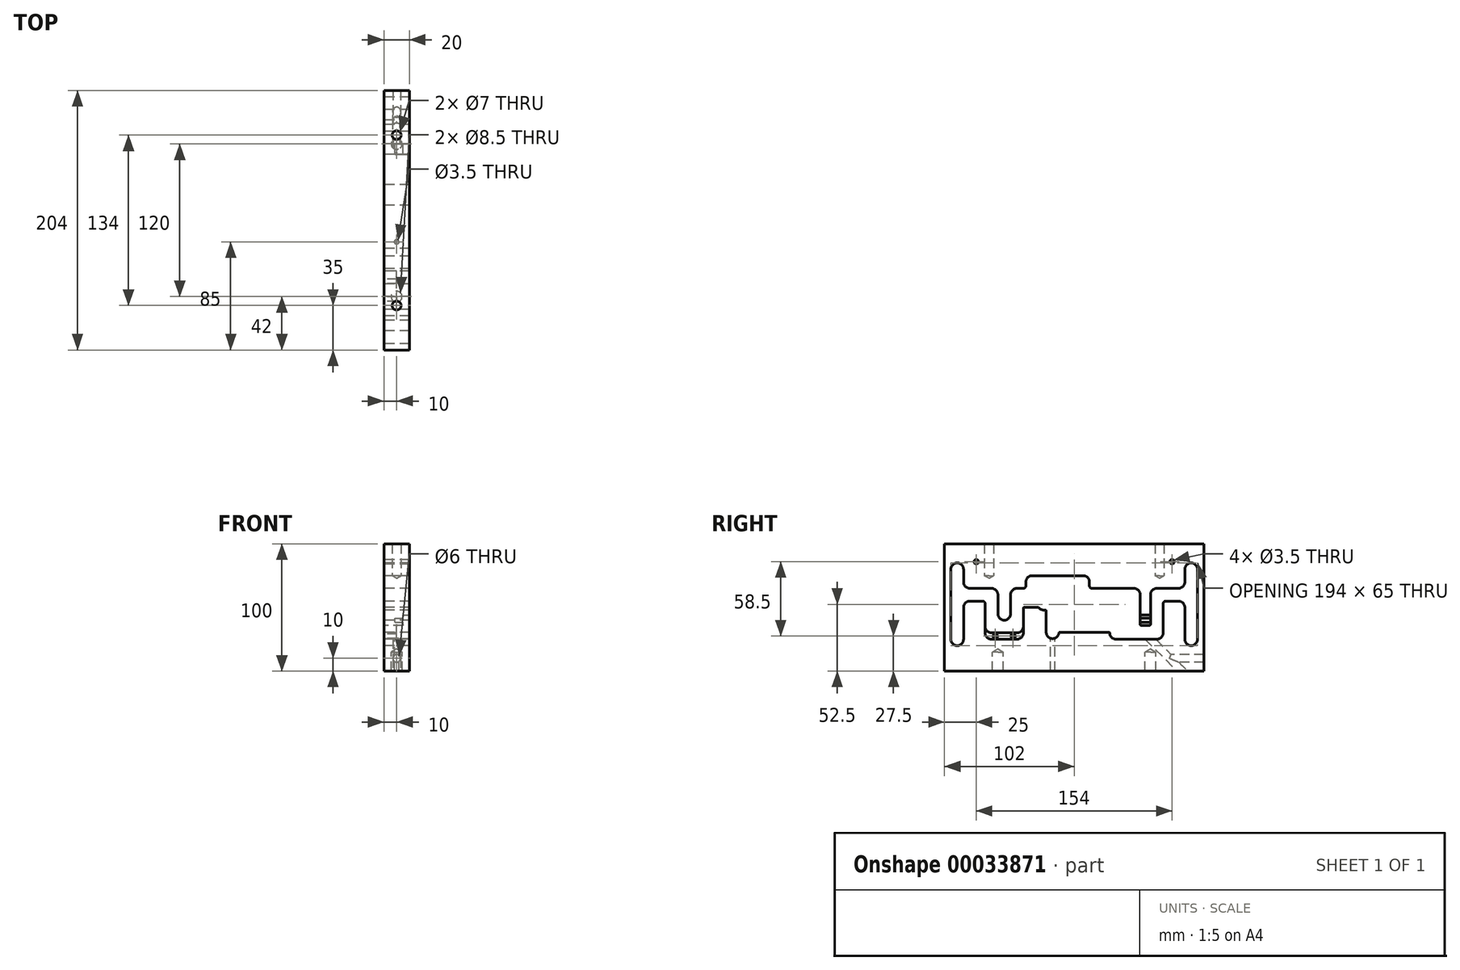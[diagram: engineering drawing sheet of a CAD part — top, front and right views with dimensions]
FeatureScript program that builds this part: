
annotation { "Feature Type Name" : "Feature", "Feature Type Description" : "" }
export const myFeature = defineFeature(function(context is Context, id is Id, definition is map)
    precondition{}
    {
        {
            var Q0;
            Q0=qCreatedBy(makeId("Right.planeOp"),FACE);
            var sketch = newSketch(context, id + "F0", { "sketchPlane" : qUnion([Q0])});
            skLineSegment(sketch, "E0.bottom", {"start": v(0, 0) * mm, "end": v(-204, 0) * mm});
            skLineSegment(sketch, "E0.top", {"start": v(0, 100) * mm, "end": v(-204, 100) * mm});
            skLineSegment(sketch, "E0.left", {"start": v(0, 0) * mm, "end": v(0, 100) * mm});
            skLineSegment(sketch, "E0.right", {"start": v(-204, 0) * mm, "end": v(-204, 100) * mm});
            skLineSegment(sketch, "E1", {"start": v(-167, 65) * mm, "end": v(-184, 65) * mm});
            skLineSegment(sketch, "E2", {"start": v(-189, 70) * mm, "end": v(-189, 80) * mm});
            skLineSegment(sketch, "E3", {"start": v(-199, 80) * mm, "end": v(-199, 25) * mm});
            skLineSegment(sketch, "E4", {"start": v(-189, 25) * mm, "end": v(-189, 50) * mm});
            skLineSegment(sketch, "E5", {"start": v(-184, 55) * mm, "end": v(-174, 55) * mm});
            skLineSegment(sketch, "E6", {"start": v(-172, 53) * mm, "end": v(-172, 30) * mm});
            skLineSegment(sketch, "E7", {"start": v(-167, 25) * mm, "end": v(-147, 25) * mm});
            skLineSegment(sketch, "E8", {"start": v(-142, 30) * mm, "end": v(-142, 49.5) * mm});
            skLineSegment(sketch, "E9", {"start": v(-114, 30.5) * mm, "end": v(-74, 30.5) * mm});
            skLineSegment(sketch, "E10", {"start": v(-69, 25) * mm, "end": v(-37, 25) * mm});
            skLineSegment(sketch, "E11", {"start": v(-32, 30) * mm, "end": v(-32, 53) * mm});
            skLineSegment(sketch, "E12", {"start": v(-30, 55) * mm, "end": v(-20, 55) * mm});
            skLineSegment(sketch, "E13", {"start": v(-15, 50) * mm, "end": v(-15, 25) * mm});
            skLineSegment(sketch, "E14", {"start": v(-5, 25) * mm, "end": v(-5, 80) * mm});
            skLineSegment(sketch, "E15", {"start": v(-15, 80) * mm, "end": v(-15, 70) * mm});
            skLineSegment(sketch, "E16", {"start": v(-20, 65) * mm, "end": v(-37, 65) * mm});
            skLineSegment(sketch, "E17", {"start": v(-42, 60) * mm, "end": v(-42, 36.5) * mm});
            skLineSegment(sketch, "E18", {"start": v(-42.5, 36) * mm, "end": v(-49.5, 36) * mm});
            skLineSegment(sketch, "E19", {"start": v(-50, 36.5) * mm, "end": v(-50, 60) * mm});
            skLineSegment(sketch, "E20", {"start": v(-152, 60) * mm, "end": v(-152, 45) * mm});
            skLineSegment(sketch, "E21", {"start": v(-162, 45) * mm, "end": v(-162, 60) * mm});
            skArc(sketch, "E22", {"start": v(-199, 25) * mm, "mid": v(-194, 20) * mm, "end": v(-189, 25) * mm});
            skArc(sketch, "E23", {"start": v(-189, 80) * mm, "mid": v(-194, 85) * mm, "end": v(-199, 80) * mm});
            skArc(sketch, "E24", {"start": v(-5, 80) * mm, "mid": v(-10, 85) * mm, "end": v(-15, 80) * mm});
            skArc(sketch, "E25", {"start": v(-15, 25) * mm, "mid": v(-10, 20) * mm, "end": v(-5, 25) * mm});
            skPoint(sketch, "E26.visualSharp", {"position": v(-189, 65) * mm});
            skArc(sketch, "E26.filletArc", {"start": v(-189, 70) * mm, "mid": v(-187.54, 66.46) * mm, "end": v(-184, 65) * mm});
            skPoint(sketch, "E27.visualSharp", {"position": v(-189, 55) * mm});
            skArc(sketch, "E27.filletArc", {"start": v(-184, 55) * mm, "mid": v(-187.54, 53.54) * mm, "end": v(-189, 50) * mm});
            skPoint(sketch, "E28.visualSharp", {"position": v(-15, 65) * mm});
            skArc(sketch, "E28.filletArc", {"start": v(-20, 65) * mm, "mid": v(-16.46, 66.46) * mm, "end": v(-15, 70) * mm});
            skPoint(sketch, "E29.visualSharp", {"position": v(-15, 55) * mm});
            skArc(sketch, "E29.filletArc", {"start": v(-15, 50) * mm, "mid": v(-16.46, 53.54) * mm, "end": v(-20, 55) * mm});
            skPoint(sketch, "E30.visualSharp", {"position": v(-162, 65) * mm});
            skArc(sketch, "E30.filletArc", {"start": v(-162, 60) * mm, "mid": v(-163.46, 63.54) * mm, "end": v(-167, 65) * mm});
            skPoint(sketch, "E31.visualSharp", {"position": v(-172, 25) * mm});
            skArc(sketch, "E31.filletArc", {"start": v(-172, 30) * mm, "mid": v(-170.54, 26.46) * mm, "end": v(-167, 25) * mm});
            skPoint(sketch, "E32.visualSharp", {"position": v(-142, 25) * mm});
            skArc(sketch, "E32.filletArc", {"start": v(-147, 25) * mm, "mid": v(-143.46, 26.46) * mm, "end": v(-142, 30) * mm});
            skArc(sketch, "E33", {"start": v(-162, 45) * mm, "mid": v(-157, 40) * mm, "end": v(-152, 45) * mm});
            skPoint(sketch, "E34.visualSharp", {"position": v(-42, 65) * mm});
            skArc(sketch, "E34.filletArc", {"start": v(-37, 65) * mm, "mid": v(-40.54, 63.54) * mm, "end": v(-42, 60) * mm});
            skLineSegment(sketch, "E35", {"start": v(-147, 65) * mm, "end": v(-142, 65) * mm});
            skLineSegment(sketch, "E36", {"start": v(-141.5, 50) * mm, "end": v(-130, 50) * mm});
            skPoint(sketch, "E37.visualSharp", {"position": v(-152, 65) * mm});
            skArc(sketch, "E37.filletArc", {"start": v(-147, 65) * mm, "mid": v(-150.54, 63.54) * mm, "end": v(-152, 60) * mm});
            skPoint(sketch, "E38.visualSharp", {"position": v(-172, 55) * mm});
            skArc(sketch, "E38.filletArc", {"start": v(-172, 53) * mm, "mid": v(-172.59, 54.41) * mm, "end": v(-174, 55) * mm});
            skPoint(sketch, "E39.visualSharp", {"position": v(-32, 55) * mm});
            skArc(sketch, "E39.filletArc", {"start": v(-30, 55) * mm, "mid": v(-31.41, 54.41) * mm, "end": v(-32, 53) * mm});
            skPoint(sketch, "E40.visualSharp", {"position": v(-32, 25) * mm});
            skArc(sketch, "E40.filletArc", {"start": v(-37, 25) * mm, "mid": v(-33.46, 26.46) * mm, "end": v(-32, 30) * mm});
            skLineSegment(sketch, "E41", {"start": v(-126, 48) * mm, "end": v(-124, 48) * mm});
            skLineSegment(sketch, "E42", {"start": v(-124, 48) * mm, "end": v(-124, 30.5) * mm});
            skArc(sketch, "E43", {"start": v(-124, 30.5) * mm, "mid": v(-119, 25.5) * mm, "end": v(-114, 30.5) * mm});
            skArc(sketch, "E44", {"start": v(-130, 50) * mm, "mid": v(-128.24, 48.53) * mm, "end": v(-126, 48) * mm});
            skLineSegment(sketch, "E45.bottom", {"start": v(-116.5, 49.5) * mm, "end": v(-63.5, 49.5) * mm, "construction": true});
            skLineSegment(sketch, "E45.top", {"start": v(-116.5, 30.5) * mm, "end": v(-63.5, 30.5) * mm, "construction": true});
            skLineSegment(sketch, "E45.left", {"start": v(-116.5, 49.5) * mm, "end": v(-116.5, 30.5) * mm, "construction": true});
            skLineSegment(sketch, "E45.right", {"start": v(-63.5, 49.5) * mm, "end": v(-63.5, 30.5) * mm, "construction": true});
            skLineSegment(sketch, "E46", {"start": v(-86.55, 40) * mm, "end": v(-38.27, 40) * mm, "construction": true});
            skPoint(sketch, "E46.startSnap0", {"position": v(-63.5, 40) * mm});
            skLineSegment(sketch, "E47", {"start": v(-74, 30.5) * mm, "end": v(-74, 30) * mm});
            skPoint(sketch, "E48.visualSharp", {"position": v(-74, 25) * mm});
            skArc(sketch, "E48.filletArc", {"start": v(-74, 30) * mm, "mid": v(-72.54, 26.46) * mm, "end": v(-69, 25) * mm});
            skPoint(sketch, "E49.visualSharp", {"position": v(-50, 65) * mm});
            skArc(sketch, "E49.filletArc", {"start": v(-50, 60) * mm, "mid": v(-51.46, 63.54) * mm, "end": v(-55, 65) * mm});
            skLineSegment(sketch, "E50", {"start": v(-135, 75) * mm, "end": v(-95, 75) * mm});
            skLineSegment(sketch, "E51", {"start": v(-90, 70) * mm, "end": v(-90, 67) * mm});
            skLineSegment(sketch, "E52", {"start": v(-140, 70) * mm, "end": v(-140, 67) * mm});
            skLineSegment(sketch, "E53.trimOffspring", {"start": v(-88, 65) * mm, "end": v(-55, 65) * mm});
            skPoint(sketch, "E54.visualSharp", {"position": v(-140, 75) * mm});
            skArc(sketch, "E54.filletArc", {"start": v(-135, 75) * mm, "mid": v(-138.54, 73.54) * mm, "end": v(-140, 70) * mm});
            skPoint(sketch, "E55.visualSharp", {"position": v(-90, 75) * mm});
            skArc(sketch, "E55.filletArc", {"start": v(-90, 70) * mm, "mid": v(-91.46, 73.54) * mm, "end": v(-95, 75) * mm});
            skPoint(sketch, "E56.visualSharp", {"position": v(-140, 65) * mm});
            skArc(sketch, "E56.filletArc", {"start": v(-142, 65) * mm, "mid": v(-140.59, 65.59) * mm, "end": v(-140, 67) * mm});
            skPoint(sketch, "E57.visualSharp", {"position": v(-90, 65) * mm});
            skArc(sketch, "E57.filletArc", {"start": v(-90, 67) * mm, "mid": v(-89.41, 65.59) * mm, "end": v(-88, 65) * mm});
            skLineSegment(sketch, "E58", {"start": v(-179, 86) * mm, "end": v(-25, 86) * mm, "construction": true});
            skCircle(sketch, "E59", {"center": v(-179, 86) * mm, "radius": 1.75 * mm});
            skCircle(sketch, "E60", {"center": v(-25, 86) * mm, "radius": 1.75 * mm});
            skLineSegment(sketch, "E61", {"start": v(-147, 30) * mm, "end": v(-167, 30) * mm});
            skPoint(sketch, "E62.visualSharp", {"position": v(-172, 30) * mm});
            skArc(sketch, "E62.filletArc", {"start": v(-172, 35) * mm, "mid": v(-170.54, 31.46) * mm, "end": v(-167, 30) * mm});
            skPoint(sketch, "E63.visualSharp", {"position": v(-142, 30) * mm});
            skArc(sketch, "E63.filletArc", {"start": v(-147, 30) * mm, "mid": v(-143.46, 31.46) * mm, "end": v(-142, 35) * mm});
            skCircle(sketch, "E64", {"center": v(-150, 27.5) * mm, "radius": 1.75 * mm});
            skCircle(sketch, "E65", {"center": v(-164, 27.5) * mm, "radius": 1.75 * mm});
            skLineSegment(sketch, "E66", {"start": v(-157, 28.47) * mm, "end": v(-157, 26.58) * mm, "construction": true});
            skPoint(sketch, "E66.startSnap0", {"position": v(-157, 30) * mm});
            skPoint(sketch, "E67.visualSharp", {"position": v(-142, 50) * mm});
            skArc(sketch, "E67.filletArc", {"start": v(-141.5, 50) * mm, "mid": v(-141.85, 49.85) * mm, "end": v(-142, 49.5) * mm});
            skPoint(sketch, "E68.visualSharp", {"position": v(-42, 36) * mm});
            skArc(sketch, "E68.filletArc", {"start": v(-42.5, 36) * mm, "mid": v(-42.15, 36.15) * mm, "end": v(-42, 36.5) * mm});
            skPoint(sketch, "E69.visualSharp", {"position": v(-50, 36) * mm});
            skArc(sketch, "E69.filletArc", {"start": v(-50, 36.5) * mm, "mid": v(-49.85, 36.15) * mm, "end": v(-49.5, 36) * mm});
            skSolve(sketch);
        }
        {
            var Q0;
            Q0 = qSketchRegion(id + "F0", true);
            extrude(context, id + "F1", {"entities" : qUnion([Q0]), "depth" : 20 * mm});
        }
        {
            var Q0;
            Q0=makeQuery(id+"F1.opExtrude","SWEPT_FACE",FACE,{"disambiguationData":[OSD([sQuery(id+"F0.wireOp",EDGE,"E0.bottom")])]});
            var sketch = newSketch(context, id + "F2", { "sketchPlane" : qUnion([Q0])});
            skPoint(sketch, "E70", {"position": v(10, 119) * mm});
            skPoint(sketch, "E70.positionSnap0", {"position": v(10, 204) * mm});
            skSolve(sketch);
        }
        {
            var Q0;
            Q0=sQuery(id+"F2.wireOp",VERTEX,"E70");
            var Q1;
            Q1=makeQuery(id+"F1.opExtrude","SWEPT_BODY",BODY,{"disambiguationData":[OSD([sQuery(id+"F0.wireOp",EDGE,"E0.bottom"),sQuery(id+"F0.wireOp",EDGE,"E0.top"),sQuery(id+"F0.wireOp",EDGE,"E0.left"),sQuery(id+"F0.wireOp",EDGE,"E0.right"),sQuery(id+"F0.wireOp",EDGE,"E1"),sQuery(id+"F0.wireOp",EDGE,"E2"),sQuery(id+"F0.wireOp",EDGE,"E3"),sQuery(id+"F0.wireOp",EDGE,"E4"),sQuery(id+"F0.wireOp",EDGE,"E5"),sQuery(id+"F0.wireOp",EDGE,"E6"),sQuery(id+"F0.wireOp",EDGE,"E7"),sQuery(id+"F0.wireOp",EDGE,"E8"),sQuery(id+"F0.wireOp",EDGE,"E9"),sQuery(id+"F0.wireOp",EDGE,"E10"),sQuery(id+"F0.wireOp",EDGE,"E11"),sQuery(id+"F0.wireOp",EDGE,"E12"),sQuery(id+"F0.wireOp",EDGE,"E13"),sQuery(id+"F0.wireOp",EDGE,"E14"),sQuery(id+"F0.wireOp",EDGE,"E15"),sQuery(id+"F0.wireOp",EDGE,"E16"),sQuery(id+"F0.wireOp",EDGE,"E17"),sQuery(id+"F0.wireOp",EDGE,"E18"),sQuery(id+"F0.wireOp",EDGE,"E19"),sQuery(id+"F0.wireOp",EDGE,"E20"),sQuery(id+"F0.wireOp",EDGE,"E21"),sQuery(id+"F0.wireOp",EDGE,"E22"),sQuery(id+"F0.wireOp",EDGE,"E23"),sQuery(id+"F0.wireOp",EDGE,"E24"),sQuery(id+"F0.wireOp",EDGE,"E25"),sQuery(id+"F0.wireOp",EDGE,"E26.filletArc"),sQuery(id+"F0.wireOp",EDGE,"E27.filletArc"),sQuery(id+"F0.wireOp",EDGE,"E28.filletArc"),sQuery(id+"F0.wireOp",EDGE,"E29.filletArc"),sQuery(id+"F0.wireOp",EDGE,"E30.filletArc"),sQuery(id+"F0.wireOp",EDGE,"E31.filletArc"),sQuery(id+"F0.wireOp",EDGE,"E32.filletArc"),sQuery(id+"F0.wireOp",EDGE,"E33"),sQuery(id+"F0.wireOp",EDGE,"E34.filletArc"),sQuery(id+"F0.wireOp",EDGE,"E35"),sQuery(id+"F0.wireOp",EDGE,"E36"),sQuery(id+"F0.wireOp",EDGE,"E37.filletArc"),sQuery(id+"F0.wireOp",EDGE,"E38.filletArc"),sQuery(id+"F0.wireOp",EDGE,"E39.filletArc"),sQuery(id+"F0.wireOp",EDGE,"E40.filletArc"),sQuery(id+"F0.wireOp",EDGE,"E41"),sQuery(id+"F0.wireOp",EDGE,"E42"),sQuery(id+"F0.wireOp",EDGE,"E43"),sQuery(id+"F0.wireOp",EDGE,"E44"),sQuery(id+"F0.wireOp",EDGE,"E47"),sQuery(id+"F0.wireOp",EDGE,"E48.filletArc"),sQuery(id+"F0.wireOp",EDGE,"E49.filletArc"),sQuery(id+"F0.wireOp",EDGE,"E50"),sQuery(id+"F0.wireOp",EDGE,"E51"),sQuery(id+"F0.wireOp",EDGE,"E52"),sQuery(id+"F0.wireOp",EDGE,"E53.trimOffspring"),sQuery(id+"F0.wireOp",EDGE,"E54.filletArc"),sQuery(id+"F0.wireOp",EDGE,"E55.filletArc"),sQuery(id+"F0.wireOp",EDGE,"E56.filletArc"),sQuery(id+"F0.wireOp",EDGE,"E57.filletArc")])]});
            hole(context, id + "F3", {"style" : HoleStyle.SIMPLE, "holeDiameter" : 3.5 * mm, "endStyle" : HoleEndStyle.BLIND, "holeDepth" : 30 * mm, "locations" : qUnion([Q0]), "scope" : qUnion([Q1])});
        }
        {
            var Q0;
            Q0=makeQuery(id+"F1.opExtrude","SWEPT_FACE",FACE,{"disambiguationData":[OSD([sQuery(id+"F0.wireOp",EDGE,"E0.top")])]});
            var sketch = newSketch(context, id + "F4", { "sketchPlane" : qUnion([Q0])});
            skPoint(sketch, "E71", {"position": v(10, -169) * mm});
            skPoint(sketch, "E71.positionSnap0", {"position": v(10, -204) * mm});
            skPoint(sketch, "E72", {"position": v(10, -35) * mm});
            skPoint(sketch, "E72.positionSnap0", {"position": v(10, 0) * mm});
            skSolve(sketch);
        }
        {
            var Q0;
            Q0=sQuery(id+"F4.wireOp",VERTEX,"E71");
            var Q1;
            Q1=sQuery(id+"F4.wireOp",VERTEX,"E72");
            var Q2;
            Q2=makeQuery(id+"F1.opExtrude","SWEPT_BODY",BODY,{"disambiguationData":[OSD([sQuery(id+"F0.wireOp",EDGE,"E0.bottom"),sQuery(id+"F0.wireOp",EDGE,"E0.top"),sQuery(id+"F0.wireOp",EDGE,"E0.left"),sQuery(id+"F0.wireOp",EDGE,"E0.right"),sQuery(id+"F0.wireOp",EDGE,"E1"),sQuery(id+"F0.wireOp",EDGE,"E2"),sQuery(id+"F0.wireOp",EDGE,"E3"),sQuery(id+"F0.wireOp",EDGE,"E4"),sQuery(id+"F0.wireOp",EDGE,"E5"),sQuery(id+"F0.wireOp",EDGE,"E6"),sQuery(id+"F0.wireOp",EDGE,"E7"),sQuery(id+"F0.wireOp",EDGE,"E8"),sQuery(id+"F0.wireOp",EDGE,"E9"),sQuery(id+"F0.wireOp",EDGE,"E10"),sQuery(id+"F0.wireOp",EDGE,"E11"),sQuery(id+"F0.wireOp",EDGE,"E12"),sQuery(id+"F0.wireOp",EDGE,"E13"),sQuery(id+"F0.wireOp",EDGE,"E14"),sQuery(id+"F0.wireOp",EDGE,"E15"),sQuery(id+"F0.wireOp",EDGE,"E16"),sQuery(id+"F0.wireOp",EDGE,"E17"),sQuery(id+"F0.wireOp",EDGE,"E18"),sQuery(id+"F0.wireOp",EDGE,"E19"),sQuery(id+"F0.wireOp",EDGE,"E20"),sQuery(id+"F0.wireOp",EDGE,"E21"),sQuery(id+"F0.wireOp",EDGE,"E22"),sQuery(id+"F0.wireOp",EDGE,"E23"),sQuery(id+"F0.wireOp",EDGE,"E24"),sQuery(id+"F0.wireOp",EDGE,"E25"),sQuery(id+"F0.wireOp",EDGE,"E26.filletArc"),sQuery(id+"F0.wireOp",EDGE,"E27.filletArc"),sQuery(id+"F0.wireOp",EDGE,"E28.filletArc"),sQuery(id+"F0.wireOp",EDGE,"E29.filletArc"),sQuery(id+"F0.wireOp",EDGE,"E30.filletArc"),sQuery(id+"F0.wireOp",EDGE,"E31.filletArc"),sQuery(id+"F0.wireOp",EDGE,"E32.filletArc"),sQuery(id+"F0.wireOp",EDGE,"E33"),sQuery(id+"F0.wireOp",EDGE,"E34.filletArc"),sQuery(id+"F0.wireOp",EDGE,"E35"),sQuery(id+"F0.wireOp",EDGE,"E36"),sQuery(id+"F0.wireOp",EDGE,"E37.filletArc"),sQuery(id+"F0.wireOp",EDGE,"E38.filletArc"),sQuery(id+"F0.wireOp",EDGE,"E39.filletArc"),sQuery(id+"F0.wireOp",EDGE,"E40.filletArc"),sQuery(id+"F0.wireOp",EDGE,"E41"),sQuery(id+"F0.wireOp",EDGE,"E42"),sQuery(id+"F0.wireOp",EDGE,"E43"),sQuery(id+"F0.wireOp",EDGE,"E44"),sQuery(id+"F0.wireOp",EDGE,"E47"),sQuery(id+"F0.wireOp",EDGE,"E48.filletArc"),sQuery(id+"F0.wireOp",EDGE,"E49.filletArc"),sQuery(id+"F0.wireOp",EDGE,"E50"),sQuery(id+"F0.wireOp",EDGE,"E51"),sQuery(id+"F0.wireOp",EDGE,"E52"),sQuery(id+"F0.wireOp",EDGE,"E53.trimOffspring"),sQuery(id+"F0.wireOp",EDGE,"E54.filletArc"),sQuery(id+"F0.wireOp",EDGE,"E55.filletArc"),sQuery(id+"F0.wireOp",EDGE,"E56.filletArc"),sQuery(id+"F0.wireOp",EDGE,"E57.filletArc")])]});
            hole(context, id + "F5", {"style" : HoleStyle.SIMPLE, "holeDiameter" : 7 * mm, "endStyle" : HoleEndStyle.BLIND, "holeDepth" : 25 * mm, "locations" : qUnion([Q0, Q1]), "scope" : qUnion([Q2])});
        }
        {
            var Q0;
            Q0=makeQuery(id+"F1.opExtrude","SWEPT_FACE",FACE,{"disambiguationData":[OSD([sQuery(id+"F0.wireOp",EDGE,"E0.left")])]});
            var sketch = newSketch(context, id + "F6", { "sketchPlane" : qUnion([Q0])});
            skPoint(sketch, "E73", {"position": v(-10, 10) * mm});
            skPoint(sketch, "E73.positionSnap0", {"position": v(-10, 0) * mm});
            skSolve(sketch);
        }
        {
            var Q0;
            Q0=sQuery(id+"F6.wireOp",VERTEX,"E73");
            var Q1;
            Q1=makeQuery(id+"F1.opExtrude","SWEPT_BODY",BODY,{"disambiguationData":[OSD([sQuery(id+"F0.wireOp",EDGE,"E0.bottom"),sQuery(id+"F0.wireOp",EDGE,"E0.top"),sQuery(id+"F0.wireOp",EDGE,"E0.left"),sQuery(id+"F0.wireOp",EDGE,"E0.right"),sQuery(id+"F0.wireOp",EDGE,"E1"),sQuery(id+"F0.wireOp",EDGE,"E2"),sQuery(id+"F0.wireOp",EDGE,"E3"),sQuery(id+"F0.wireOp",EDGE,"E4"),sQuery(id+"F0.wireOp",EDGE,"E5"),sQuery(id+"F0.wireOp",EDGE,"E6"),sQuery(id+"F0.wireOp",EDGE,"E7"),sQuery(id+"F0.wireOp",EDGE,"E8"),sQuery(id+"F0.wireOp",EDGE,"E9"),sQuery(id+"F0.wireOp",EDGE,"E10"),sQuery(id+"F0.wireOp",EDGE,"E11"),sQuery(id+"F0.wireOp",EDGE,"E12"),sQuery(id+"F0.wireOp",EDGE,"E13"),sQuery(id+"F0.wireOp",EDGE,"E14"),sQuery(id+"F0.wireOp",EDGE,"E15"),sQuery(id+"F0.wireOp",EDGE,"E16"),sQuery(id+"F0.wireOp",EDGE,"E17"),sQuery(id+"F0.wireOp",EDGE,"E18"),sQuery(id+"F0.wireOp",EDGE,"E19"),sQuery(id+"F0.wireOp",EDGE,"E20"),sQuery(id+"F0.wireOp",EDGE,"E21"),sQuery(id+"F0.wireOp",EDGE,"E22"),sQuery(id+"F0.wireOp",EDGE,"E23"),sQuery(id+"F0.wireOp",EDGE,"E24"),sQuery(id+"F0.wireOp",EDGE,"E25"),sQuery(id+"F0.wireOp",EDGE,"E26.filletArc"),sQuery(id+"F0.wireOp",EDGE,"E27.filletArc"),sQuery(id+"F0.wireOp",EDGE,"E28.filletArc"),sQuery(id+"F0.wireOp",EDGE,"E29.filletArc"),sQuery(id+"F0.wireOp",EDGE,"E30.filletArc"),sQuery(id+"F0.wireOp",EDGE,"E31.filletArc"),sQuery(id+"F0.wireOp",EDGE,"E32.filletArc"),sQuery(id+"F0.wireOp",EDGE,"E33"),sQuery(id+"F0.wireOp",EDGE,"E34.filletArc"),sQuery(id+"F0.wireOp",EDGE,"E35"),sQuery(id+"F0.wireOp",EDGE,"E36"),sQuery(id+"F0.wireOp",EDGE,"E37.filletArc"),sQuery(id+"F0.wireOp",EDGE,"E38.filletArc"),sQuery(id+"F0.wireOp",EDGE,"E39.filletArc"),sQuery(id+"F0.wireOp",EDGE,"E40.filletArc"),sQuery(id+"F0.wireOp",EDGE,"E41"),sQuery(id+"F0.wireOp",EDGE,"E42"),sQuery(id+"F0.wireOp",EDGE,"E43"),sQuery(id+"F0.wireOp",EDGE,"E44"),sQuery(id+"F0.wireOp",EDGE,"E47"),sQuery(id+"F0.wireOp",EDGE,"E48.filletArc"),sQuery(id+"F0.wireOp",EDGE,"E49.filletArc"),sQuery(id+"F0.wireOp",EDGE,"E50"),sQuery(id+"F0.wireOp",EDGE,"E51"),sQuery(id+"F0.wireOp",EDGE,"E52"),sQuery(id+"F0.wireOp",EDGE,"E53.trimOffspring"),sQuery(id+"F0.wireOp",EDGE,"E54.filletArc"),sQuery(id+"F0.wireOp",EDGE,"E55.filletArc"),sQuery(id+"F0.wireOp",EDGE,"E56.filletArc"),sQuery(id+"F0.wireOp",EDGE,"E57.filletArc")])]});
            hole(context, id + "F7", {"style" : HoleStyle.SIMPLE, "holeDiameter" : 6 * mm, "endStyle" : HoleEndStyle.BLIND, "holeDepth" : 27 * mm, "locations" : qUnion([Q0]), "scope" : qUnion([Q1])});
        }
        {
            var Q0;
            Q0=makeQuery(id+"F1.opExtrude","SWEPT_EDGE",EDGE,{"disambiguationData":[OSD([sQuery(id+"F0.wireOp",EDGE,"E0.bottom"),sQuery(id+"F0.wireOp",EDGE,"E0.left")])]});
            cPlane(context, id + "F8", {"entities" : qUnion([Q0]), "cplaneType" : CPlaneType.LINE_ANGLE, "offset" : 150 * mm, "angle" : 45 * degree, "width" : 150 * mm, "height" : 150 * mm});
        }
        {
            var Q0;
            Q0=qCreatedBy(id+"F8.planeOp",FACE);
            var sketch = newSketch(context, id + "F9", { "sketchPlane" : qUnion([Q0])});
            skCircle(sketch, "E74", {"center": v(10, -12) * mm, "radius": 3 * mm});
            skSolve(sketch);
        }
        {
            var Q0;
            Q0=makeQuery(id+"F9.imprint","IMPRINT",FACE,{"disambiguationData":[TD([[makeQuery(id+"F9.imprint","IMPRINT",EDGE,{"derivedFrom":sQuery(id+"F9.wireOp",EDGE,"E74")}),1.0]])]});
            extrude(context, id + "F10", {"entities" : qUnion([Q0]), "operationType" : NewBodyOperationType.REMOVE, "depth" : 60 * mm});
        }
        {
            var Q0;
            Q0=makeQuery(id+"F1.opExtrude","SWEPT_FACE",FACE,{"disambiguationData":[OSD([sQuery(id+"F0.wireOp",EDGE,"E0.bottom")])]});
            var sketch = newSketch(context, id + "F11", { "sketchPlane" : qUnion([Q0])});
            skPoint(sketch, "E75", {"position": v(10, 42) * mm});
            skPoint(sketch, "E75.positionSnap0", {"position": v(10, 12.73) * mm});
            skPoint(sketch, "E76", {"position": v(10, 162) * mm});
            skPoint(sketch, "E76.positionSnap0", {"position": v(10, 204) * mm});
            skSolve(sketch);
        }
        {
            var Q0;
            Q0=sQuery(id+"F11.wireOp",VERTEX,"E76");
            var Q1;
            Q1=sQuery(id+"F11.wireOp",VERTEX,"E75");
            var Q2;
            Q2=makeQuery(id+"F1.opExtrude","SWEPT_BODY",BODY,{"disambiguationData":[OSD([sQuery(id+"F0.wireOp",EDGE,"E0.bottom"),sQuery(id+"F0.wireOp",EDGE,"E0.top"),sQuery(id+"F0.wireOp",EDGE,"E0.left"),sQuery(id+"F0.wireOp",EDGE,"E0.right"),sQuery(id+"F0.wireOp",EDGE,"E1"),sQuery(id+"F0.wireOp",EDGE,"E2"),sQuery(id+"F0.wireOp",EDGE,"E3"),sQuery(id+"F0.wireOp",EDGE,"E4"),sQuery(id+"F0.wireOp",EDGE,"E5"),sQuery(id+"F0.wireOp",EDGE,"E6"),sQuery(id+"F0.wireOp",EDGE,"E7"),sQuery(id+"F0.wireOp",EDGE,"E8"),sQuery(id+"F0.wireOp",EDGE,"E9"),sQuery(id+"F0.wireOp",EDGE,"E10"),sQuery(id+"F0.wireOp",EDGE,"E11"),sQuery(id+"F0.wireOp",EDGE,"E12"),sQuery(id+"F0.wireOp",EDGE,"E13"),sQuery(id+"F0.wireOp",EDGE,"E14"),sQuery(id+"F0.wireOp",EDGE,"E15"),sQuery(id+"F0.wireOp",EDGE,"E16"),sQuery(id+"F0.wireOp",EDGE,"E17"),sQuery(id+"F0.wireOp",EDGE,"E18"),sQuery(id+"F0.wireOp",EDGE,"E19"),sQuery(id+"F0.wireOp",EDGE,"E20"),sQuery(id+"F0.wireOp",EDGE,"E21"),sQuery(id+"F0.wireOp",EDGE,"E22"),sQuery(id+"F0.wireOp",EDGE,"E23"),sQuery(id+"F0.wireOp",EDGE,"E24"),sQuery(id+"F0.wireOp",EDGE,"E25"),sQuery(id+"F0.wireOp",EDGE,"E26.filletArc"),sQuery(id+"F0.wireOp",EDGE,"E27.filletArc"),sQuery(id+"F0.wireOp",EDGE,"E28.filletArc"),sQuery(id+"F0.wireOp",EDGE,"E29.filletArc"),sQuery(id+"F0.wireOp",EDGE,"E30.filletArc"),sQuery(id+"F0.wireOp",EDGE,"E31.filletArc"),sQuery(id+"F0.wireOp",EDGE,"E32.filletArc"),sQuery(id+"F0.wireOp",EDGE,"E33"),sQuery(id+"F0.wireOp",EDGE,"E34.filletArc"),sQuery(id+"F0.wireOp",EDGE,"E35"),sQuery(id+"F0.wireOp",EDGE,"E36"),sQuery(id+"F0.wireOp",EDGE,"E37.filletArc"),sQuery(id+"F0.wireOp",EDGE,"E38.filletArc"),sQuery(id+"F0.wireOp",EDGE,"E39.filletArc"),sQuery(id+"F0.wireOp",EDGE,"E40.filletArc"),sQuery(id+"F0.wireOp",EDGE,"E41"),sQuery(id+"F0.wireOp",EDGE,"E42"),sQuery(id+"F0.wireOp",EDGE,"E43"),sQuery(id+"F0.wireOp",EDGE,"E44"),sQuery(id+"F0.wireOp",EDGE,"E47"),sQuery(id+"F0.wireOp",EDGE,"E48.filletArc"),sQuery(id+"F0.wireOp",EDGE,"E49.filletArc"),sQuery(id+"F0.wireOp",EDGE,"E50"),sQuery(id+"F0.wireOp",EDGE,"E51"),sQuery(id+"F0.wireOp",EDGE,"E52"),sQuery(id+"F0.wireOp",EDGE,"E53.trimOffspring"),sQuery(id+"F0.wireOp",EDGE,"E54.filletArc"),sQuery(id+"F0.wireOp",EDGE,"E55.filletArc"),sQuery(id+"F0.wireOp",EDGE,"E56.filletArc"),sQuery(id+"F0.wireOp",EDGE,"E57.filletArc")])]});
            hole(context, id + "F12", {"style" : HoleStyle.SIMPLE, "holeDiameter" : 8.5 * mm, "endStyle" : HoleEndStyle.BLIND, "holeDepth" : 15 * mm, "locations" : qUnion([Q0, Q1]), "scope" : qUnion([Q2])});
        }
        {
            var Q0;
            Q0=makeQuery(id+"F0.imprint","IMPRINT",FACE,{"disambiguationData":[TD([[makeQuery(id+"F0.imprint","IMPRINT",EDGE,{"derivedFrom":sQuery(id+"F0.wireOp",EDGE,"E7")}),1.0]])]});
            extrude(context, id + "F13", {"entities" : qUnion([Q0]), "operationType" : NewBodyOperationType.ADD, "depth" : 10 * mm});
        }
        {
            var Q0;
            Q0=makeQuery(id+"F1.opExtrude","CAP_FACE",FACE,{"disambiguationData":[OSD([sQuery(id+"F0.wireOp",EDGE,"E0.bottom"),sQuery(id+"F0.wireOp",EDGE,"E0.top"),sQuery(id+"F0.wireOp",EDGE,"E0.left"),sQuery(id+"F0.wireOp",EDGE,"E0.right"),sQuery(id+"F0.wireOp",EDGE,"E1"),sQuery(id+"F0.wireOp",EDGE,"E2"),sQuery(id+"F0.wireOp",EDGE,"E3"),sQuery(id+"F0.wireOp",EDGE,"E4"),sQuery(id+"F0.wireOp",EDGE,"E5"),sQuery(id+"F0.wireOp",EDGE,"E6"),sQuery(id+"F0.wireOp",EDGE,"E7"),sQuery(id+"F0.wireOp",EDGE,"E8"),sQuery(id+"F0.wireOp",EDGE,"E9"),sQuery(id+"F0.wireOp",EDGE,"E10"),sQuery(id+"F0.wireOp",EDGE,"E11"),sQuery(id+"F0.wireOp",EDGE,"E12"),sQuery(id+"F0.wireOp",EDGE,"E13"),sQuery(id+"F0.wireOp",EDGE,"E14"),sQuery(id+"F0.wireOp",EDGE,"E15"),sQuery(id+"F0.wireOp",EDGE,"E16"),sQuery(id+"F0.wireOp",EDGE,"E17"),sQuery(id+"F0.wireOp",EDGE,"E18"),sQuery(id+"F0.wireOp",EDGE,"E19"),sQuery(id+"F0.wireOp",EDGE,"E20"),sQuery(id+"F0.wireOp",EDGE,"E21"),sQuery(id+"F0.wireOp",EDGE,"E22"),sQuery(id+"F0.wireOp",EDGE,"E23"),sQuery(id+"F0.wireOp",EDGE,"E24"),sQuery(id+"F0.wireOp",EDGE,"E25"),sQuery(id+"F0.wireOp",EDGE,"E26.filletArc"),sQuery(id+"F0.wireOp",EDGE,"E27.filletArc"),sQuery(id+"F0.wireOp",EDGE,"E28.filletArc"),sQuery(id+"F0.wireOp",EDGE,"E29.filletArc"),sQuery(id+"F0.wireOp",EDGE,"E30.filletArc"),sQuery(id+"F0.wireOp",EDGE,"E31.filletArc"),sQuery(id+"F0.wireOp",EDGE,"E32.filletArc"),sQuery(id+"F0.wireOp",EDGE,"E33"),sQuery(id+"F0.wireOp",EDGE,"E34.filletArc"),sQuery(id+"F0.wireOp",EDGE,"E35"),sQuery(id+"F0.wireOp",EDGE,"E36"),sQuery(id+"F0.wireOp",EDGE,"E37.filletArc"),sQuery(id+"F0.wireOp",EDGE,"E38.filletArc"),sQuery(id+"F0.wireOp",EDGE,"E39.filletArc"),sQuery(id+"F0.wireOp",EDGE,"E40.filletArc"),sQuery(id+"F0.wireOp",EDGE,"E41"),sQuery(id+"F0.wireOp",EDGE,"E42"),sQuery(id+"F0.wireOp",EDGE,"E43"),sQuery(id+"F0.wireOp",EDGE,"E44"),sQuery(id+"F0.wireOp",EDGE,"E47"),sQuery(id+"F0.wireOp",EDGE,"E48.filletArc"),sQuery(id+"F0.wireOp",EDGE,"E49.filletArc"),sQuery(id+"F0.wireOp",EDGE,"E50"),sQuery(id+"F0.wireOp",EDGE,"E51"),sQuery(id+"F0.wireOp",EDGE,"E52"),sQuery(id+"F0.wireOp",EDGE,"E53.trimOffspring"),sQuery(id+"F0.wireOp",EDGE,"E54.filletArc"),sQuery(id+"F0.wireOp",EDGE,"E55.filletArc"),sQuery(id+"F0.wireOp",EDGE,"E56.filletArc"),sQuery(id+"F0.wireOp",EDGE,"E57.filletArc"),sQuery(id+"F0.wireOp",EDGE,"E59"),sQuery(id+"F0.wireOp",EDGE,"E60")])],"isStart":false});
            var sketch = newSketch(context, id + "F14", { "sketchPlane" : qUnion([Q0])});
            skLineSegment(sketch, "E77.bottom", {"start": v(-50, 36) * mm, "end": v(-42, 36) * mm});
            skLineSegment(sketch, "E77.top", {"start": v(-50, 44) * mm, "end": v(-42, 44) * mm});
            skLineSegment(sketch, "E77.left", {"start": v(-50, 36) * mm, "end": v(-50, 44) * mm});
            skLineSegment(sketch, "E77.right", {"start": v(-42, 36) * mm, "end": v(-42, 44) * mm});
            skLineSegment(sketch, "E78.bottom", {"start": v(-50, 41.5) * mm, "end": v(-42, 41.5) * mm});
            skLineSegment(sketch, "E78.top", {"start": v(-50, 38.5) * mm, "end": v(-42, 38.5) * mm});
            skLineSegment(sketch, "E78.left", {"start": v(-50, 41.5) * mm, "end": v(-50, 38.5) * mm});
            skLineSegment(sketch, "E78.right", {"start": v(-42, 41.5) * mm, "end": v(-42, 38.5) * mm});
            skPoint(sketch, "E79", {"position": v(-42, 40) * mm});
            skSolve(sketch);
        }
        {
            var Q0;
            Q0 = qSketchRegion(id + "F14", true);
            extrude(context, id + "F15", {"entities" : qUnion([Q0]), "operationType" : NewBodyOperationType.REMOVE, "oppositeDirection" : true, "depth" : 5 * mm});
        }
        {
            var Q0;
            Q0=makeQuery(id+"F14.imprint","IMPRINT",FACE,{"disambiguationData":[TD([[makeQuery(id+"F14.imprint","IMPRINT",EDGE,{"derivedFrom":sQuery(id+"F14.wireOp",EDGE,"E78.bottom")}),-1.0]])]});
            extrude(context, id + "F16", {"entities" : qUnion([Q0]), "operationType" : NewBodyOperationType.REMOVE, "oppositeDirection" : true, "depth" : 11.4 * mm});
        }
        {
            var Q0;
            Q0=makeQuery(id+"F1.opExtrude","SWEPT_EDGE",EDGE,{"disambiguationData":[OSD([sQuery(id+"F0.wireOp",EDGE,"E41"),sQuery(id+"F0.wireOp",EDGE,"E42")])]});
            fillet(context, id + "F17", {"entities" : qUnion([Q0]), "radius" : 0.5 * mm, "tangentPropagation" : true, "allowEdgeOverflow" : false});
        }
        {
            var Q0;
            Q0=makeQuery(id+"F1.opExtrude","SWEPT_EDGE",EDGE,{"disambiguationData":[OSD([sQuery(id+"F0.wireOp",EDGE,"E9"),sQuery(id+"F0.wireOp",EDGE,"E43")])]});
            fillet(context, id + "F18", {"entities" : qUnion([Q0]), "radius" : 0.5 * mm, "tangentPropagation" : true, "allowEdgeOverflow" : false});
        }
        {
            var Q0;
            Q0=makeQuery(id+"F1.opExtrude","SWEPT_EDGE",EDGE,{"disambiguationData":[OSD([sQuery(id+"F0.wireOp",EDGE,"E9"),sQuery(id+"F0.wireOp",EDGE,"E47")])]});
            fillet(context, id + "F19", {"entities" : qUnion([Q0]), "radius" : 0.5 * mm, "tangentPropagation" : true, "allowEdgeOverflow" : false});
        }
    });
